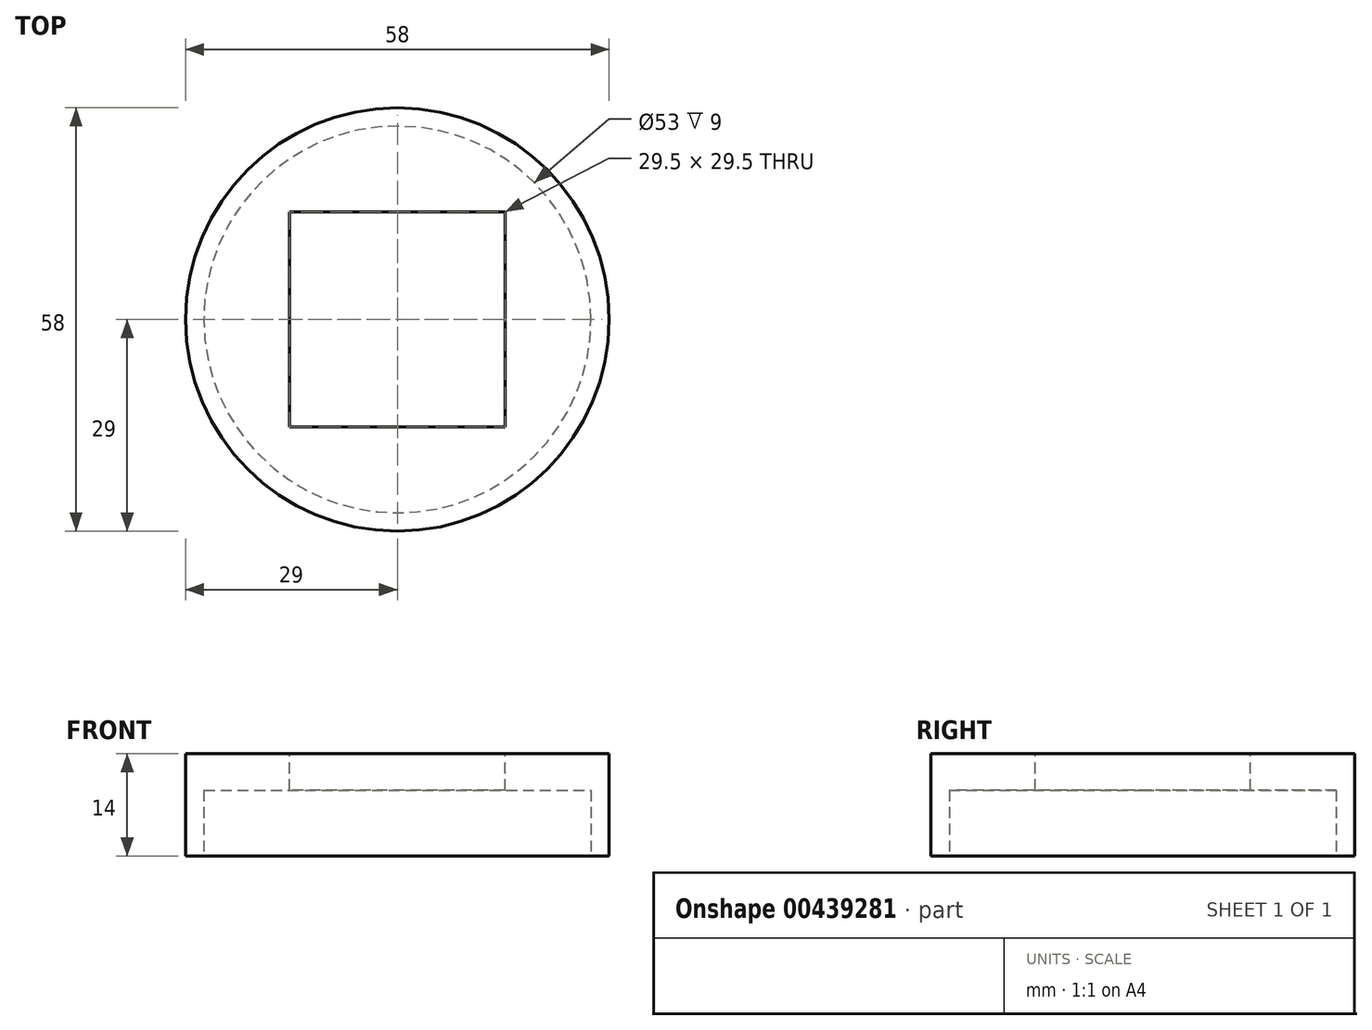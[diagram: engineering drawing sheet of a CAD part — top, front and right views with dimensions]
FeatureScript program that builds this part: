
annotation { "Feature Type Name" : "Feature", "Feature Type Description" : "" }
export const myFeature = defineFeature(function(context is Context, id is Id, definition is map)
    precondition{}
    {
        {
            var Q0;
            Q0=qCreatedBy(makeId("Top.planeOp"),FACE);
            var sketch = newSketch(context, id + "F0", { "sketchPlane" : qUnion([Q0])});
            skCircle(sketch, "E0", {"center": v(0, 0) * mm, "radius": 29 * mm});
            skSolve(sketch);
        }
        {
            var Q0;
            Q0 = qSketchRegion(id + "F0", true);
            extrude(context, id + "F1", {"entities" : qUnion([Q0]), "depth" : 14 * mm});
        }
        {
            var Q0;
            Q0=makeQuery(id+"F1.opExtrude","CAP_FACE",FACE,{"disambiguationData":[OSD([sQuery(id+"F0.wireOp",EDGE,"E0")])],"isStart":false});
            var sketch = newSketch(context, id + "F2", { "sketchPlane" : qUnion([Q0])});
            skLineSegment(sketch, "E1.bottom", {"start": v(14.75, 14.75) * mm, "end": v(-14.75, 14.75) * mm});
            skLineSegment(sketch, "E1.top", {"start": v(14.75, -14.75) * mm, "end": v(-14.75, -14.75) * mm});
            skLineSegment(sketch, "E1.left", {"start": v(14.75, 14.75) * mm, "end": v(14.75, -14.75) * mm});
            skLineSegment(sketch, "E1.right", {"start": v(-14.75, 14.75) * mm, "end": v(-14.75, -14.75) * mm});
            skPoint(sketch, "E1.middle", {"position": v(0, 0) * mm});
            skSolve(sketch);
        }
        {
            var Q0;
            Q0 = qSketchRegion(id + "F2", true);
            extrude(context, id + "F3", {"entities" : qUnion([Q0]), "operationType" : NewBodyOperationType.REMOVE, "oppositeDirection" : true, "depth" : 25 * mm});
        }
        {
            var Q0;
            Q0=makeQuery(id+"F1.opExtrude","CAP_FACE",FACE,{"disambiguationData":[OSD([sQuery(id+"F0.wireOp",EDGE,"E0")])],"isStart":true});
            var sketch = newSketch(context, id + "F4", { "sketchPlane" : qUnion([Q0])});
            skCircle(sketch, "E2", {"center": v(0, 0) * mm, "radius": 26.5 * mm});
            skSolve(sketch);
        }
        {
            var Q0;
            Q0 = qSketchRegion(id + "F4", true);
            extrude(context, id + "F5", {"entities" : qUnion([Q0]), "operationType" : NewBodyOperationType.REMOVE, "oppositeDirection" : true, "depth" : 9 * mm});
        }
    });
